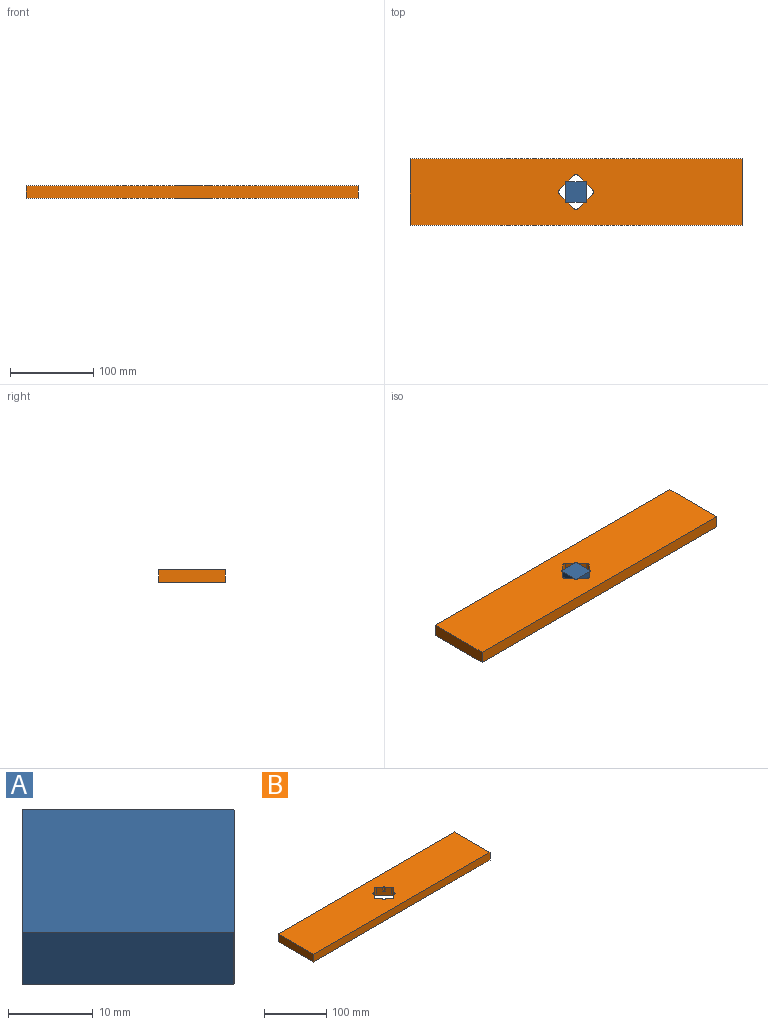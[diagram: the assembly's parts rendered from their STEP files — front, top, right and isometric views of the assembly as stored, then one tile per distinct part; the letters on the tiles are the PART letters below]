
ASSEMBLY  parts=2 mates=1
PART A: 10 faces, bbox 35.3x35.3x7.5 mm
  f0: plane 17.61x17.61mm, normal (-0.71,0.71,0), area 186.7mm2, adj f1,f7,f8,f9
  f1: cylinder r=0.05mm len=7.5mm, axis (0,0,1), area 0.6mm2, adj f0,f2,f8,f9
  f2: plane 17.61x17.61mm, normal (0.71,0.71,0), area 186.7mm2, adj f1,f3,f8,f9
  f3: cylinder r=0.05mm len=7.5mm, axis (0,0,1), area 0.6mm2, adj f2,f4,f8,f9
  f4: plane 17.61x17.61mm, normal (0.71,-0.71,0), area 186.7mm2, adj f3,f5,f8,f9
  f5: cylinder r=0.05mm len=7.5mm, axis (0,0,1), area 0.6mm2, adj f4,f6,f8,f9
  f6: plane 17.61x17.61mm, normal (-0.71,-0.71,0), area 186.7mm2, adj f5,f7,f8,f9
  f7: cylinder r=0.05mm len=7.5mm, axis (0,0,1), area 0.6mm2, adj f0,f6,f8,f9
  f8: plane 35.31x35.31mm, normal (0,0,-1), area 625mm2, adj f0,f1,f2,f3,f4,f5,f6,f7
  f9: plane 35.31x35.31mm, normal (0,0,1), area 625mm2, adj f0,f1,f2,f3,f4,f5,f6,f7
PART B: 30 faces, bbox 400x80x15 mm
  f0: plane 17.61x17.61mm, normal (-0.71,-0.71,0), area 335.5mm2, adj f4,f6,f10,f11,f26,f28,f29
  f1: plane 17.61x17.61mm, normal (-0.71,0.71,0), area 335.5mm2, adj f4,f6,f11,f12,f22,f24,f25
  f2: plane 17.61x17.61mm, normal (0.71,0.71,0), area 335.5mm2, adj f4,f6,f12,f13,f18,f20,f21
  f3: plane 17.61x17.61mm, normal (0.71,-0.71,0), area 335.5mm2, adj f4,f6,f10,f13,f14,f16,f17
  f4: plane 400x80mm, normal (0,0,-1), area 30986.8mm2, adj f0,f1,f2,f3,f5,f7,f8,f9
  f5: plane 80x15mm, normal (-1,0,0), area 1200mm2, adj f4,f6,f7,f8
  f6: plane 400x80mm, normal (0,0,1), area 30967.8mm2, adj f0,f1,f2,f3,f5,f7,f8,f9
  f7: plane 400x15mm, normal (0,1,0), area 6000mm2, adj f4,f5,f6,f9
  f8: plane 400x15mm, normal (0,-1,0), area 6000mm2, adj f4,f5,f6,f9
  f9: plane 80x15mm, normal (1,0,0), area 1200mm2, adj f4,f6,f7,f8
  f10: cylinder r=3.55mm len=15mm, axis (0,0,1), area 83.6mm2, adj f0,f3,f4,f6
  f11: cylinder r=3.55mm len=15mm, axis (0,0,1), area 83.6mm2, adj f0,f1,f4,f6
  f12: cylinder r=3.55mm len=15mm, axis (0,0,1), area 83.6mm2, adj f1,f2,f4,f6
  f13: cylinder r=3.55mm len=15mm, axis (0,0,1), area 83.6mm2, adj f2,f3,f4,f6
  f14: plane 3.58x3.58mm, normal (0,0,1), area 4.8mm2, adj f3,f15,f16,f17
  f15: cylinder r=1.75mm len=7.5mm, axis (0,0,1), area 30.7mm2, adj f6,f14,f16,f17
  f16: cylinder r=1mm len=7.5mm, axis (0,0,1), area 8.8mm2, adj f3,f6,f14,f15
  f17: cylinder r=1mm len=7.5mm, axis (0,0,1), area 8.8mm2, adj f3,f6,f14,f15
  f18: plane 3.58x3.58mm, normal (0,0,1), area 4.8mm2, adj f2,f19,f20,f21
  f19: cylinder r=1.75mm len=7.5mm, axis (0,0,1), area 30.7mm2, adj f6,f18,f20,f21
  f20: cylinder r=1mm len=7.5mm, axis (0,0,1), area 8.8mm2, adj f2,f6,f18,f19
  f21: cylinder r=1mm len=7.5mm, axis (0,0,1), area 8.8mm2, adj f2,f6,f18,f19
  f22: plane 3.58x3.58mm, normal (0,0,1), area 4.8mm2, adj f1,f23,f24,f25
  f23: cylinder r=1.75mm len=7.5mm, axis (0,0,1), area 30.7mm2, adj f6,f22,f24,f25
  f24: cylinder r=1mm len=7.5mm, axis (0,0,1), area 8.8mm2, adj f1,f6,f22,f23
  f25: cylinder r=1mm len=7.5mm, axis (0,0,1), area 8.8mm2, adj f1,f6,f22,f23
  f26: plane 3.58x3.58mm, normal (0,0,1), area 4.8mm2, adj f0,f27,f28,f29
  f27: cylinder r=1.75mm len=7.5mm, axis (0,0,1), area 30.7mm2, adj f6,f26,f28,f29
  f28: cylinder r=1mm len=7.5mm, axis (0,0,1), area 8.8mm2, adj f0,f6,f26,f27
  f29: cylinder r=1mm len=7.5mm, axis (0,0,1), area 8.8mm2, adj f0,f6,f26,f27
PLACE A rot(axis=(0,0,1),45deg) t=(0,0,7.5)mm
PLACE B at identity fixed
MATE fastened A.f8 <-> B.f14  axis (0,0,1) through (0,0,-7.5)mm
